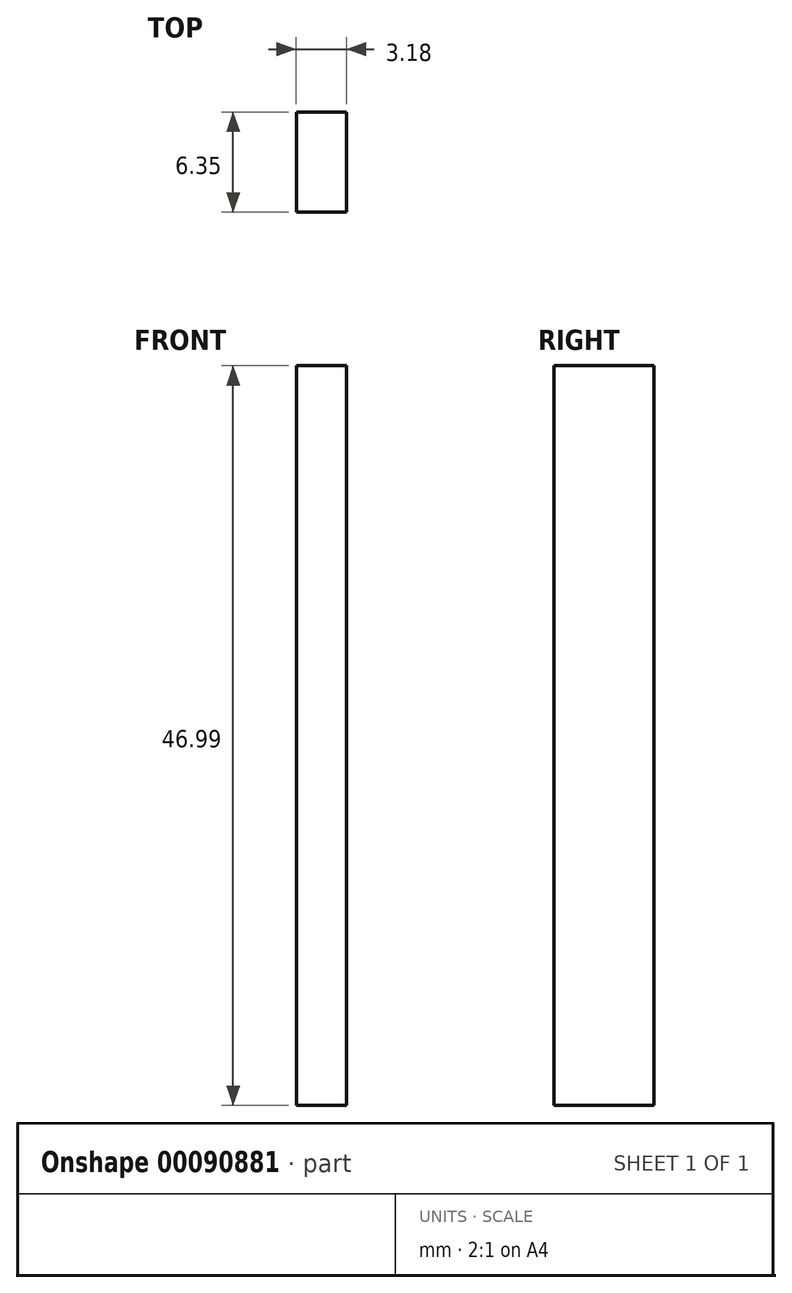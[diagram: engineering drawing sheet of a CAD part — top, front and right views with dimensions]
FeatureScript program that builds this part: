
annotation { "Feature Type Name" : "Feature", "Feature Type Description" : "" }
export const myFeature = defineFeature(function(context is Context, id is Id, definition is map)
    precondition{}
    {
        {
            var Q0;
            Q0=qCreatedBy(makeId("Right.planeOp"),FACE);
            var sketch = newSketch(context, id + "F0", { "sketchPlane" : qUnion([Q0])});
            skLineSegment(sketch, "E0.bottom", {"start": v(-14.8, 21.88) * mm, "end": v(-8.46, 21.88) * mm});
            skLineSegment(sketch, "E0.top", {"start": v(-14.8, -25.11) * mm, "end": v(-8.46, -25.11) * mm});
            skLineSegment(sketch, "E0.left", {"start": v(-14.8, 21.88) * mm, "end": v(-14.8, -25.11) * mm});
            skLineSegment(sketch, "E0.right", {"start": v(-8.46, 21.88) * mm, "end": v(-8.46, -25.11) * mm});
            skSolve(sketch);
        }
        {
            var Q0;
            Q0 = qSketchRegion(id + "F0", true);
            extrude(context, id + "F1", {"entities" : qUnion([Q0]), "endBound" : BoundingType.SYMMETRIC, "depth" : 3.17 * mm});
        }
    });
